# Revit family: 208_UELA-_
name_source: partatom
category: Air Terminals
units: mm (PartAtom-declared; Revit-internal decimal feet)

## family parameters
Always vertical = Yes
Cut with Voids When Loaded = No
Part Type = Normal
Room Calculation Point = Yes
Round Connector Dimension = Use Diameter
Shared = No
Work Plane-Based = No

## types (5) — shared parameters
CAT0 = Yes
CL_Location_5000 = 5000 mm  [stored 16.4042 ft]
Description = CHROME NICKEL-PLATED AIR INTAKE WALL MOUNTED WITH MOUNTING FRAME
L1 = 20 mm  [stored 0.0656168 ft]
L1__ve = -20 mm  [stored -0.0656168 ft]
L_ARR = 400 mm  [stored 1.31234 ft]
Manufacturer = Alnor
QmdConnectorList = 201;D
URL = http://www.ventilation-alnor.co.uk
W_ARR = 400 mm  [stored 1.31234 ft]
XRefLineVPlnId = 7453
YRefLineVPlnId = 7456
magiPartTypeId = 208
magiProductFamilyId = UELA-*
zero-valued in all types: CLBTZ, H_ARR

## per-type parameters (varying)
| type | D | DAF | R | magiProductId |
| UELA 100 | 100 mm | 173 mm  [stored 0.567585 ft] | 49 mm | UELA-100 |
| UELA 200 | 200 mm | 293 mm | 98 mm | UELA-200 |
| UELA 160 | 160 mm | 232 mm | 78 mm | UELA-160 |
| UELA 150 | 150 mm | 232 mm | 73 mm | UELA-150 |
| UELA 125 | 125 mm | 205 mm | 60 mm | UELA-125 |

note: column(s) folded — value = type name in every type: MC Product Code

note: [stored X ft] marks values corroborated as IEEE doubles in the binary element streams (Revit-internal decimal feet)

## geometry (parser evidence)
native form markers: Blend x4, Sweep x1
no freeform markers — native parametric forms only
